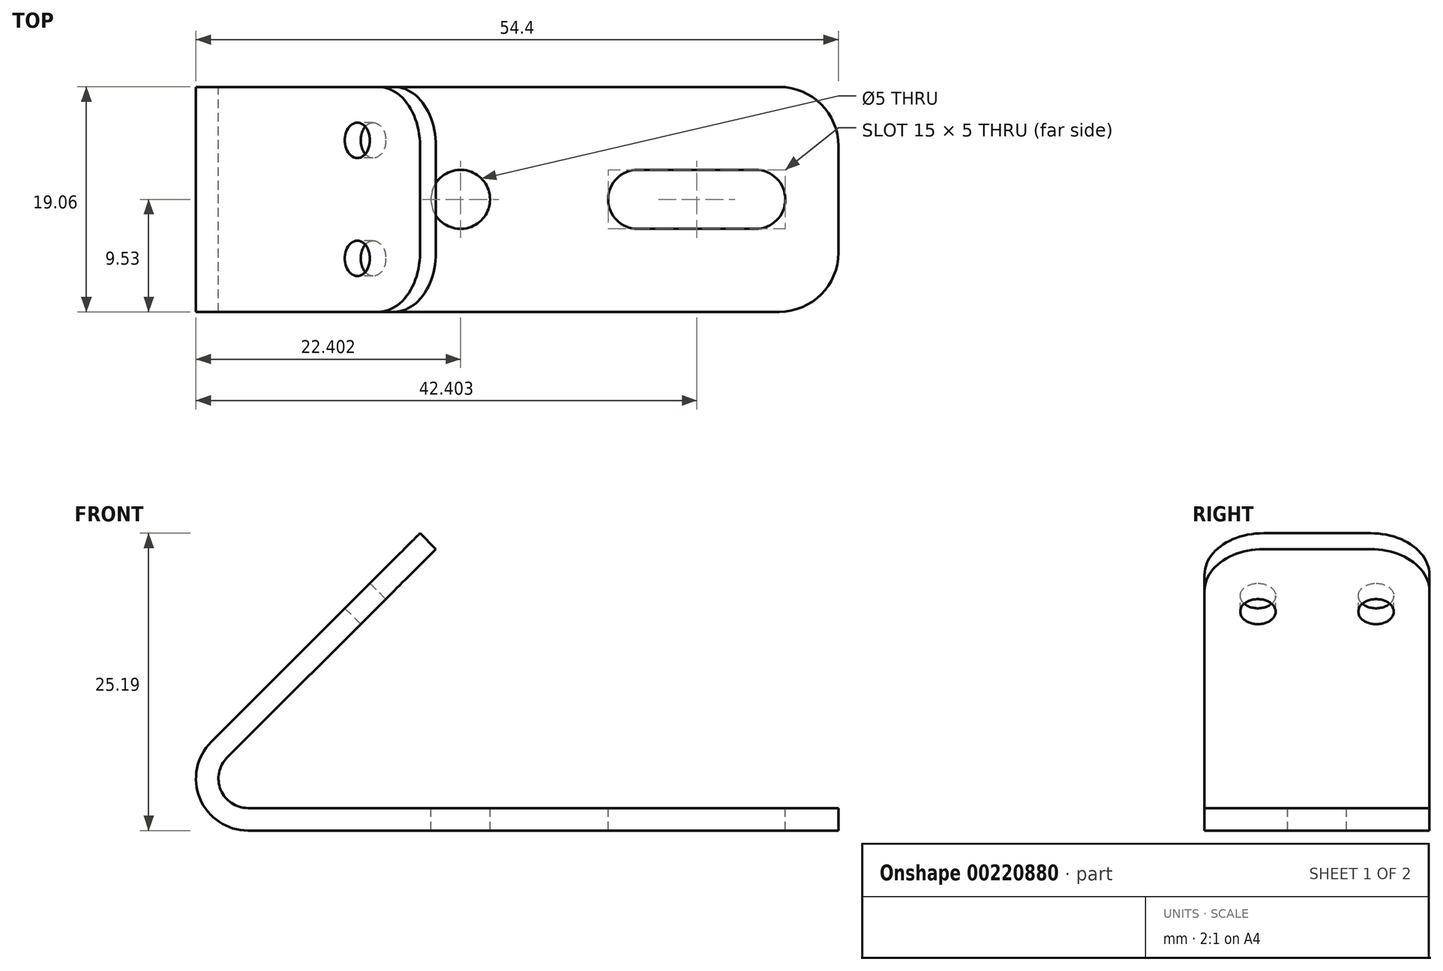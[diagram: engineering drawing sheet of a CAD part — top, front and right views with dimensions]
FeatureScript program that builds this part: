
annotation { "Feature Type Name" : "Feature", "Feature Type Description" : "" }
export const myFeature = defineFeature(function(context is Context, id is Id, definition is map)
    precondition{}
    {
        {
            var Q0;
            Q0=qCreatedBy(makeId("Front.planeOp"),FACE);
            var sketch = newSketch(context, id + "F0", { "sketchPlane" : qUnion([Q0])});
            skLineSegment(sketch, "E0", {"start": v(25.19, 25.19) * mm, "end": v(7.51, 7.51) * mm});
            skLineSegment(sketch, "E1", {"start": v(10.62, 0) * mm, "end": v(60.62, 0) * mm});
            skPoint(sketch, "E2.visualSharp", {"position": v(0, 0) * mm});
            skArc(sketch, "E2.filletArc", {"start": v(7.51, 7.51) * mm, "mid": v(6.56, 2.72) * mm, "end": v(10.62, 0) * mm});
            skLineSegment(sketch, "E3.0", {"start": v(10.62, 1.9) * mm, "end": v(60.62, 1.9) * mm});
            skArc(sketch, "E3.1", {"start": v(8.85, 6.17) * mm, "mid": v(8.31, 3.44) * mm, "end": v(10.62, 1.9) * mm});
            skLineSegment(sketch, "E3.2", {"start": v(26.53, 23.85) * mm, "end": v(8.85, 6.17) * mm});
            skLineSegment(sketch, "E4", {"start": v(25.19, 25.19) * mm, "end": v(26.53, 23.85) * mm});
            skLineSegment(sketch, "E5", {"start": v(60.62, 1.9) * mm, "end": v(60.62, 0) * mm});
            skSolve(sketch);
        }
        {
            var Q0;
            Q0=qSketchRegion(id+"F0",true);
            extrude(context, id + "F1", {"entities" : qUnion([Q0]), "endBound" : BoundingType.SYMMETRIC, "depth" : 19.05 * mm});
        }
        {
            var Q0;
            Q0=makeQuery(id+"F1.opExtrude","CAP_EDGE",EDGE,{"disambiguationData":[OSD([sQuery(id+"F0.wireOp",EDGE,"E4")])],"isStart":false});
            var Q1;
            Q1=makeQuery(id+"F1.opExtrude","CAP_EDGE",EDGE,{"disambiguationData":[OSD([sQuery(id+"F0.wireOp",EDGE,"E4")])],"isStart":true});
            var Q2;
            Q2=makeQuery(id+"F1.opExtrude","CAP_EDGE",EDGE,{"disambiguationData":[OSD([sQuery(id+"F0.wireOp",EDGE,"E5")])],"isStart":true});
            var Q3;
            Q3=makeQuery(id+"F1.opExtrude","CAP_EDGE",EDGE,{"disambiguationData":[OSD([sQuery(id+"F0.wireOp",EDGE,"E5")])],"isStart":false});
            fillet(context, id + "F2", {"entities" : qUnion([Q0, Q1, Q2, Q3]), "radius" : 5 * mm, "tangentPropagation" : true, "allowEdgeOverflow" : false});
        }
        {
            var Q0;
            Q0=makeQuery(id+"F1.opExtrude","SWEPT_FACE",FACE,{"disambiguationData":[OSD([sQuery(id+"F0.wireOp",EDGE,"E0")])]});
            var sketch = newSketch(context, id + "F3", { "sketchPlane" : qUnion([Q0])});
            skLineSegment(sketch, "E6.top", {"start": v(5, 28.12) * mm, "end": v(-5, 28.12) * mm, "construction": true});
            skPoint(sketch, "E6.middle", {"position": v(0, 0) * mm});
            skCircle(sketch, "E7", {"center": v(-5, 28.12) * mm, "radius": 1.5 * mm});
            skCircle(sketch, "E8", {"center": v(5, 28.12) * mm, "radius": 1.5 * mm});
            skLineSegment(sketch, "E9", {"start": v(0, 0) * mm, "end": v(0, 28.12) * mm, "construction": true});
            skSolve(sketch);
        }
        {
            var Q0;
            Q0=qSketchRegion(id+"F3",true);
            extrude(context, id + "F4", {"entities" : qUnion([Q0]), "operationType" : NewBodyOperationType.REMOVE, "endBound" : BoundingType.UP_TO_NEXT, "oppositeDirection" : true, "depth" : 25.4 * mm});
        }
        {
            var Q0;
            Q0=makeQuery(id+"F1.opExtrude","SWEPT_FACE",FACE,{"disambiguationData":[OSD([sQuery(id+"F0.wireOp",EDGE,"E3.0")])]});
            var sketch = newSketch(context, id + "F5", { "sketchPlane" : qUnion([Q0])});
            skCircle(sketch, "E10", {"center": v(28.62, 0) * mm, "radius": 2.5 * mm});
            skLineSegment(sketch, "E11", {"start": v(43.62, 0) * mm, "end": v(53.62, 0) * mm});
            skArc(sketch, "E12.0.startCap", {"start": v(43.62, -2.5) * mm, "mid": v(41.12, 0) * mm, "end": v(43.62, 2.5) * mm});
            skArc(sketch, "E12.0.endCap", {"start": v(53.62, 2.5) * mm, "mid": v(56.12, 0) * mm, "end": v(53.62, -2.5) * mm});
            skLineSegment(sketch, "E12.0.left", {"start": v(43.62, 2.5) * mm, "end": v(53.62, 2.5) * mm});
            skLineSegment(sketch, "E12.0.right", {"start": v(43.62, -2.5) * mm, "end": v(53.62, -2.5) * mm});
            skSolve(sketch);
        }
        {
            var Q0;
            Q0=qSketchRegion(id+"F5",true);
            extrude(context, id + "F6", {"entities" : qUnion([Q0]), "operationType" : NewBodyOperationType.REMOVE, "endBound" : BoundingType.THROUGH_ALL, "oppositeDirection" : true, "depth" : 25.4 * mm});
        }
    });
